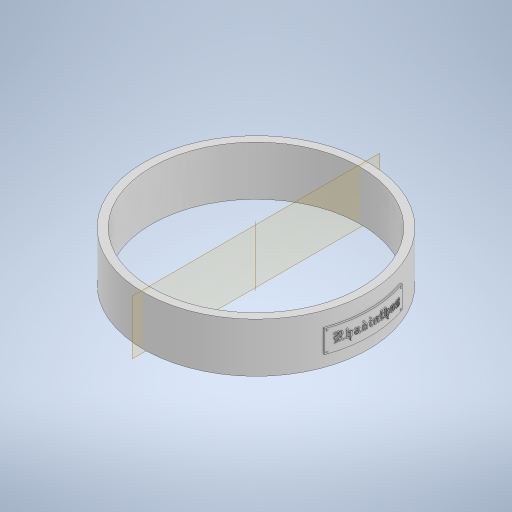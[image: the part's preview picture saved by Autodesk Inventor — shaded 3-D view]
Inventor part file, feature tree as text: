
AUTODESK INVENTOR PART (.ipt)
format: ipt  version: 2023 (Build 270158000, 158)  size: 4,644,352 bytes
history: native  units: in
note: dims shown in document units (in); Inventor stores cm internally (conversion verified against a paired STEP export)
features: emboss x3, pattern_circular x3, other x2, extrude x1, plane x1, fillet x1, sketch x1
ambient origin geometry x8: Origin, YZ Plane, XZ Plane, XY Plane, X Axis, Y Axis, Z Axis, Center Point
bodies: Solid1 (feature_tree)
feature tree (12):
  extrude  "Extrusion1"  Depth=0.3937in
  plane  "Work Plane1"
  other  "Text"
  emboss  "Emboss4"
  emboss  "Emboss5"
  emboss  "Emboss6"
  fillet  "Rivots"  Radius=0.8661in
  pattern_circular  "Circular Pattern1"  Count=6  [1 undecoded]
  pattern_circular  "Circular Pattern2"  [2 undecoded]
  pattern_circular  "Circular Pattern3"  [2 undecoded]
  sketch  "Sketch1"  dims[d0=3.937in d1=3.6614in d2=0.8661in d3=0.0in d4=2.3622in d6=0.4546in d10=0.0in d11=0.3937in d12=1.378in d19=0.0in d20=0.0in d21=0.0295in d22=0.0in d23=0.0197in d24=0.0in d25=0.0295in d26=0.0295in d27=0.0295in d28=0.0157in d29=0.0in d30=0.0138in d31=0.7874in d32=360.0deg d34=0.7874in d35=360.0deg d37=0.7874in d38=360.0deg d33=0.0in]
  other  "NamePlate"
note: 5 required parameter values undecoded (feature->parameter linkage not recoverable at this tier; creation-order binding heuristic only, values carry confidence <= 0.55)
